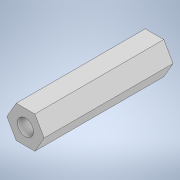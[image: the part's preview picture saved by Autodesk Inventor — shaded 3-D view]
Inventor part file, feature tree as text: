
AUTODESK INVENTOR PART (.ipt)
format: ipt  version: 2021 (Build 250183000, 183)  size: 100,352 bytes
history: native  units: mm
features: extrude x2, sketch x2
ambient origin geometry x8: Origin, YZ Plane, XZ Plane, XY Plane, X Axis, Y Axis, Z Axis, Center Point
bodies: Solid1 (feature_tree)
feature tree (4):
  extrude  "Extrusion1"  Depth=20.0mm TaperAngle=0.0deg
  extrude  "Extrusion3"  Depth=7.0mm TaperAngle=0.0deg
  sketch  "Sketch1"  dims[d0=5.0mm d1=20.0mm d2=0.0mm]
  sketch  "Sketch3"  dims[d6=2.5mm d7=7.0mm d8=0.0mm]
